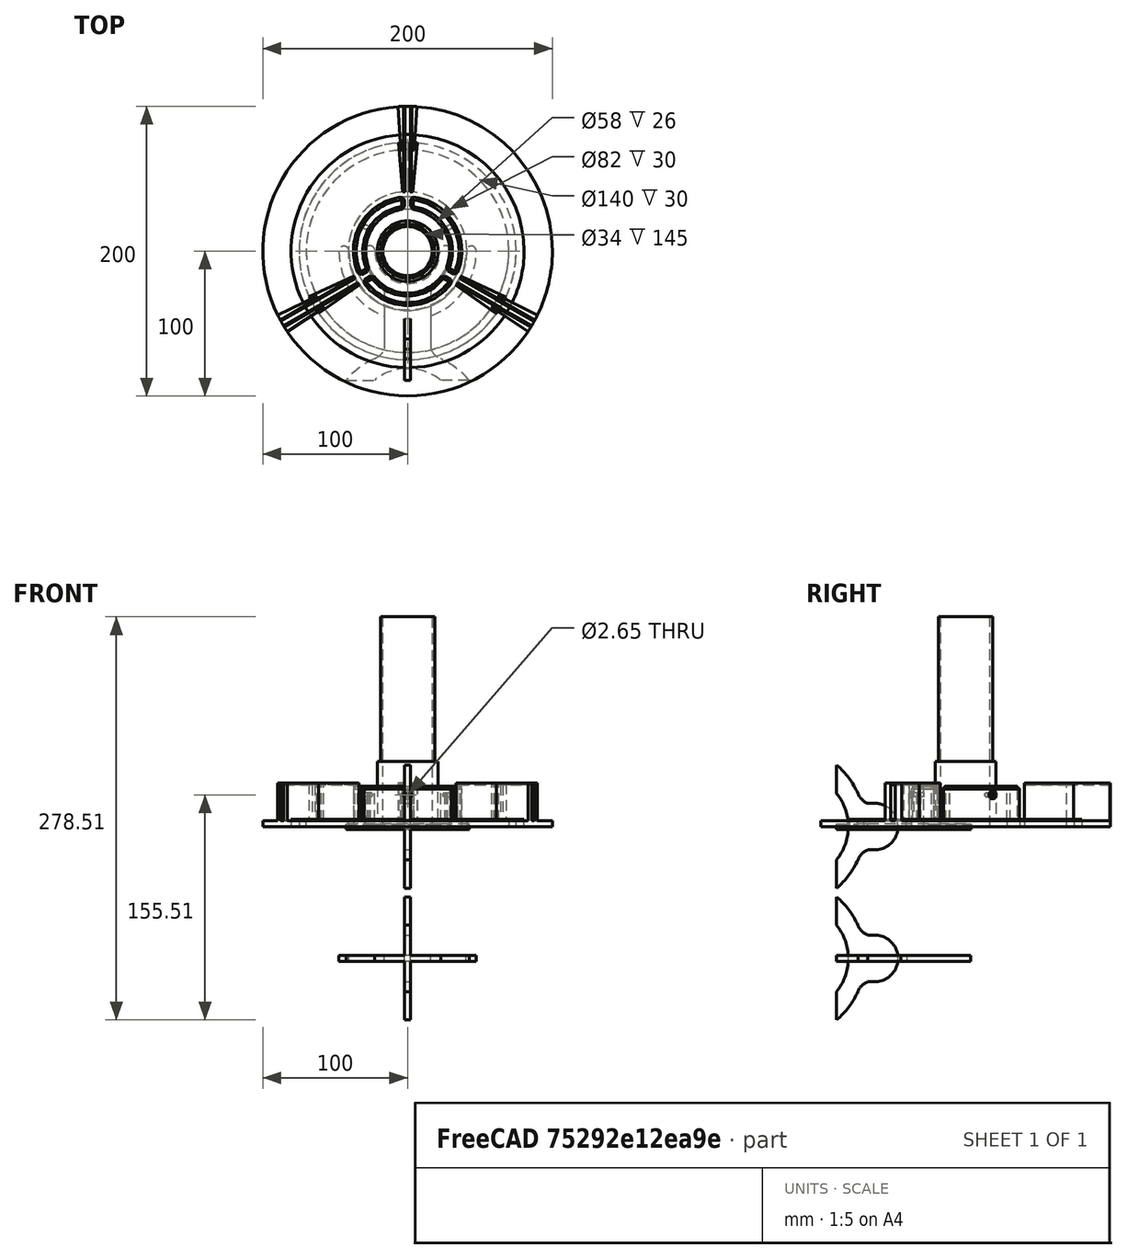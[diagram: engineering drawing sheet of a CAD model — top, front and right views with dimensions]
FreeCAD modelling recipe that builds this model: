
FCSTD DOCUMENT  (FreeCAD 1.0R39109 (Git))
Label: Madcow 3in Fiberglass Scooter Utility Set
License: All rights reserved
LicenseURL: http://en.wikipedia.org/wiki/All_rights_reserved
objects: Sketcher::SketchObject×23, PartDesign::Pocket×12, PartDesign::Pad×11, PartDesign::Body×9, App::Part×7, PartDesign::PolarPattern×6, PartDesign::Chamfer×6, PartDesign::Plane×2, Mesh::Feature×1
note: 156 computed .brp shape members not serialized (recipe doc carries the construction recipe); baked Part::Feature solids carry a one-line shape summary decoded from their .brp

FEATURE [Sketcher::SketchObject] Sketch
  ArcFitTolerance = 1e-06
  AttachmentSupport = -> [XY_Plane001]
  FullyConstrained = true
  MakeInternals = false
  MapMode = 5
  sketch-geometry (1):
    g0: Circle CenterX=0 CenterY=0 CenterZ=0 NormalX=0 NormalY=0 NormalZ=1 AngleXU=0 Radius=75
  constraints (2):
    c: Coincident(g0,g-1)
    c: Diameter(g0) = 150
FEATURE [PartDesign::Pad] Pad
  Direction = (0,0,1)
  Length = 30
  Length2 = 10
  Profile = -> Sketch
  ReferenceAxis = -> Sketch [N_Axis]
  Suppressed = false
  Type = 0
FEATURE [Sketcher::SketchObject] Sketch001
  ArcFitTolerance = 1e-06
  AttachmentSupport = -> [Pad]
  FullyConstrained = true
  MakeInternals = false
  MapMode = 5
  Placement = pos=(0,0,30) rot=(0,0,1;0rad)
  sketch-geometry (1):
    g0: Circle CenterX=0 CenterY=0 CenterZ=0 NormalX=0 NormalY=0 NormalZ=1 AngleXU=0 Radius=41
  constraints (2):
    c: Coincident(g0,g-1)
    c: Diameter(g0) = 82
FEATURE [PartDesign::Pocket] Pocket
  BaseFeature = -> Pad
  Direction = (0,0,-1)
  Length = 5
  Length2 = 5
  Profile = -> Sketch001
  ReferenceAxis = -> Sketch001 [N_Axis]
  Suppressed = false
  Type = 2
FEATURE [Sketcher::SketchObject] Sketch002
  ArcFitTolerance = 1e-06
  AttachmentSupport = -> [Pocket]
  FullyConstrained = false
  MakeInternals = false
  MapMode = 5
  Placement = pos=(0,0,30) rot=(0,0,1;0rad)
  sketch-geometry (4):
    g0: LineSegment StartX=-1.78365 StartY=75.7102 StartZ=0 EndX=-1.78365 EndY=37.8034 EndZ=0
    g1: LineSegment StartX=-1.78365 StartY=37.8034 StartZ=0 EndX=1.71635 EndY=37.8034 EndZ=0
    g2: LineSegment StartX=1.71635 StartY=37.8034 StartZ=0 EndX=1.71635 EndY=75.7102 EndZ=0
    g3: LineSegment StartX=1.71635 StartY=75.7102 StartZ=0 EndX=-1.78365 EndY=75.7102 EndZ=0
  constraints (9):
    c: Coincident(g0,g1)
    c: Coincident(g1,g2)
    c: Coincident(g2,g3)
    c: Coincident(g3,g0)
    c: Vertical(g0)
    c: Vertical(g2)
    c: Horizontal(g1)
    c: Horizontal(g3)
    c: DistanceX(g0,g2) = 3.5
FEATURE [PartDesign::Pocket] Pocket001
  BaseFeature = -> Pocket
  Direction = (0,0,-1)
  Length = 26
  Length2 = 5
  Profile = -> Sketch002
  ReferenceAxis = -> Sketch002 [N_Axis]
  Suppressed = false
  Type = 0
FEATURE [Sketcher::SketchObject] Sketch004
  ArcFitTolerance = 1e-06
  AttachmentSupport = -> [XY_Plane003]
  FullyConstrained = false
  MakeInternals = false
  MapMode = 5
  sketch-geometry (6):
    g0: Circle CenterX=0 CenterY=0 CenterZ=0 NormalX=0 NormalY=0 NormalZ=1 AngleXU=0 Radius=37.5
    g1: GeomPoint [constr] X=17.1424 Y=9.89717 Z=0
    g2: LineSegment [constr] StartX=0 StartY=0 StartZ=0 EndX=17.1424 EndY=9.89717 EndZ=0
    g3: LineSegment [constr] StartX=17.1424 StartY=9.89717 StartZ=0 EndX=32.476 EndY=18.75 EndZ=0
    g4: GeomPoint X=32.476 Y=18.75 Z=0
    g5: ArcOfCircle [constr] CenterX=0 CenterY=0 CenterZ=0 NormalX=0 NormalY=0 NormalZ=1 AngleXU=0 Radius=19.7943 StartAngle=0.523599 EndAngle=1.5708
  constraints (12):
    c: Coincident(g0,g-1)
    c: Diameter(g0) = 75
    c: Coincident(g2,g0)
    c: Coincident(g2,g1)
    c: Coincident(g3,g1)
    c: PointOnObject(g4,g0)
    c: Coincident(g3,g4)
    c: Coincident(g5,g0)
    c: Coincident(g5,g1)
    c: PointOnObject(g5,g-2)
    c: Perpendicular(g5,g3)
    c: Angle(g5) = 1.0472
FEATURE [PartDesign::Pad] Pad001
  Direction = (0,0,1)
  Length = 28
  Length2 = 10
  Profile = -> Sketch004
  ReferenceAxis = -> Sketch004 [N_Axis]
  Suppressed = false
  Type = 0
FEATURE [Sketcher::SketchObject] Sketch005
  ArcFitTolerance = 1e-06
  AttachmentSupport = -> [Pad001]
  FullyConstrained = true
  MakeInternals = false
  MapMode = 5
  Placement = pos=(0,0,28) rot=(0,0,1;0rad)
  sketch-geometry (1):
    g0: Circle CenterX=0 CenterY=0 CenterZ=0 NormalX=0 NormalY=0 NormalZ=1 AngleXU=0 Radius=29
  constraints (2):
    c: Coincident(g0,g-1)
    c: Diameter(g0) = 58
FEATURE [PartDesign::Pocket] Pocket003
  BaseFeature = -> Pad001
  Direction = (0,0,-1)
  Length = 5
  Length2 = 5
  Profile = -> Sketch005
  ReferenceAxis = -> Sketch005 [N_Axis]
  Suppressed = false
  Type = 2
FEATURE [Sketcher::SketchObject] Sketch006
  ArcFitTolerance = 1e-06
  AttachmentSupport = -> [Pocket003]
  FullyConstrained = false
  MakeInternals = false
  MapMode = 5
  Placement = pos=(0,0,28) rot=(0,0,1;0rad)
  sketch-geometry (4):
    g0: LineSegment StartX=-2.12501 StartY=38.7432 StartZ=0 EndX=-2.12501 EndY=23.0064 EndZ=0
    g1: LineSegment StartX=-2.12501 StartY=23.0064 StartZ=0 EndX=1.87499 EndY=23.0064 EndZ=0
    g2: LineSegment StartX=1.87499 StartY=23.0064 StartZ=0 EndX=1.87499 EndY=38.7432 EndZ=0
    g3: LineSegment StartX=1.87499 StartY=38.7432 StartZ=0 EndX=-2.12501 EndY=38.7432 EndZ=0
  constraints (9):
    c: Coincident(g0,g1)
    c: Coincident(g1,g2)
    c: Coincident(g2,g3)
    c: Coincident(g3,g0)
    c: Vertical(g0)
    c: Vertical(g2)
    c: Horizontal(g1)
    c: Horizontal(g3)
    c: DistanceX(g0,g2) = 4
FEATURE [PartDesign::Pocket] Pocket004
  BaseFeature = -> Pocket003
  Direction = (0,0,-1)
  Length = 24
  Length2 = 5
  Profile = -> Sketch006
  ReferenceAxis = -> Sketch006 [N_Axis]
  Suppressed = false
  Type = 0
FEATURE [PartDesign::PolarPattern] PolarPattern002
  Angle = 360
  Axis = -> Sketch006 [N_Axis]
  BaseFeature = -> Pocket004
  Mode = 0
  Occurrences = 3
  Offset = 120
  Originals = -> [Pocket004]
  Suppressed = false
  TransformMode = 0
FEATURE [PartDesign::Plane] DatumPlane
  AttachmentSupport = -> [Pocket003,Sketch004]
  Length = 117.19
  MapMode = 6
  Placement = pos=(32.476,18.75,0) rot=(0.377964,0.654654,0.654654;2.41886rad)
  ResizeMode = 0
  Width = 67.7376
FEATURE [Sketcher::SketchObject] Sketch007
  ArcFitTolerance = 1e-06
  AttachmentSupport = -> [DatumPlane]
  FullyConstrained = true
  MakeInternals = false
  MapMode = 5
  Placement = pos=(32.476,18.75,0) rot=(0.377964,0.654654,0.654654;2.41886rad)
  sketch-geometry (1):
    g0: Circle CenterX=0 CenterY=22 CenterZ=0 NormalX=0 NormalY=0 NormalZ=1 AngleXU=0 Radius=1.325
  constraints (3):
    c: PointOnObject(g0,g-2)
    c: Diameter(g0) = 2.65
    c: DistanceY(g-1,g0) = 22
FEATURE [PartDesign::Pocket] Pocket005
  BaseFeature = -> PolarPattern002
  Direction = (-0.866025,-0.5,1e-16)
  Length = 5
  Length2 = 5
  Profile = -> Sketch007
  ReferenceAxis = -> Sketch007 [N_Axis]
  Suppressed = false
  Type = 2
FEATURE [PartDesign::Chamfer] Chamfer
  Angle = 45
  Base = -> Pocket005 [Face7,Face3,Face11,Edge4,Edge6,Edge32,Edge37,Edge14,Edge12,Edge40,Edge44,Edge24,Edge29,Edge8,Edge10]
  BaseFeature = -> Pocket005
  ChamferType = 0
  FlipDirection = false
  Size = 2
  Size2 = 1
  SupportTransform = false
  Suppressed = false
  UseAllEdges = false
FEATURE [PartDesign::Chamfer] Chamfer001
  Angle = 45
  Base = -> Chamfer [Edge23]
  BaseFeature = -> Chamfer
  ChamferType = 0
  FlipDirection = false
  Size = 1.5
  Size2 = 1
  SupportTransform = false
  Suppressed = false
  UseAllEdges = false
FEATURE [PartDesign::PolarPattern] PolarPattern003
  Angle = 360
  Axis = -> Z_Axis003
  BaseFeature = -> Chamfer001
  Mode = 0
  Occurrences = 3
  Offset = 120
  Originals = -> [Pocket005,Chamfer001]
  Suppressed = false
  TransformMode = 0
FEATURE [PartDesign::Body] Body001
  AllowCompound = false
  Group = -> [Sketch004,Pad001,Sketch005,Pocket003,Sketch006,Pocket004,PolarPattern002,DatumPlane,Sketch007,Pocket005,Chamfer,Chamfer001,PolarPattern003]
  Origin = -> Origin003
  Tip = -> PolarPattern003
FEATURE [App::Part] Part001  label="Rear Rail Button Ring"
  Group = -> [Body001]
  Origin = -> Origin002
  Placement = pos=(0,0,17.3) rot=(0,0,1;0.532325rad)
FEATURE [Sketcher::SketchObject] Sketch008
  ArcFitTolerance = 1e-06
  AttachmentSupport = -> [XY_Plane005]
  FullyConstrained = false
  MakeInternals = false
  MapMode = 5
  sketch-geometry (2):
    g0: Circle CenterX=0 CenterY=0 CenterZ=0 NormalX=0 NormalY=0 NormalZ=1 AngleXU=0 Radius=38
    g1: GeomPoint X=32.9263 Y=-18.9699 Z=0
  constraints (3):
    c: Coincident(g0,g-1)
    c: Diameter(g0) = 76
    c: PointOnObject(g1,g0)
FEATURE [PartDesign::Pad] Pad002
  Direction = (0,0,1)
  Length = 20
  Length2 = 10
  Profile = -> Sketch008 [Edge1]
  ReferenceAxis = -> Sketch008 [N_Axis]
  Suppressed = false
  Type = 0
FEATURE [Sketcher::SketchObject] Sketch009
  ArcFitTolerance = 1e-06
  AttachmentSupport = -> [Pad002]
  FullyConstrained = true
  MakeInternals = false
  MapMode = 5
  Placement = pos=(0,0,20) rot=(0,0,1;0rad)
  sketch-geometry (1):
    g0: Circle CenterX=0 CenterY=0 CenterZ=0 NormalX=0 NormalY=0 NormalZ=1 AngleXU=0 Radius=29
  constraints (2):
    c: Coincident(g0,g-1)
    c: Diameter(g0) = 58
FEATURE [PartDesign::Pocket] Pocket006
  BaseFeature = -> Pad002
  Direction = (0,0,-1)
  Length = 5
  Length2 = 5
  Profile = -> Sketch009
  ReferenceAxis = -> Sketch009 [N_Axis]
  Suppressed = false
  Type = 2
FEATURE [PartDesign::Chamfer] Chamfer002
  Angle = 45
  Base = -> Pocket006 [Edge5,Edge4]
  BaseFeature = -> Pocket006
  ChamferType = 0
  FlipDirection = false
  Size = 4
  Size2 = 1
  SupportTransform = false
  Suppressed = false
  UseAllEdges = false
FEATURE [PartDesign::Plane] DatumPlane001
  AttachmentSupport = -> [Pad002,Sketch008]
  Length = 118.064
  MapMode = 6
  Placement = pos=(32.9263,-18.9699,0) rot=(0.774269,0.447497,0.447497;1.82389rad)
  ResizeMode = 0
  Width = 64.3989
FEATURE [Sketcher::SketchObject] Sketch010
  ArcFitTolerance = 1e-06
  AttachmentSupport = -> [DatumPlane001]
  FullyConstrained = false
  MakeInternals = false
  MapMode = 5
  Placement = pos=(32.9263,-18.9699,0) rot=(0.774269,0.447497,0.447497;1.82389rad)
  sketch-geometry (1):
    g0: Circle CenterX=0 CenterY=9.48073 CenterZ=0 NormalX=0 NormalY=0 NormalZ=1 AngleXU=0 Radius=1.325
  constraints (2):
    c: PointOnObject(g0,g-2)
    c: Diameter(g0) = 2.65
FEATURE [PartDesign::Pocket] Pocket007
  BaseFeature = -> Chamfer002
  Direction = (-0.866482,0.499208,1e-16)
  Length = 5
  Length2 = 5
  Profile = -> Sketch010
  ReferenceAxis = -> Sketch010 [N_Axis]
  Suppressed = false
  Type = 1
FEATURE [PartDesign::Chamfer] Chamfer003
  Angle = 45
  Base = -> Pocket007 [Edge8,Edge7]
  BaseFeature = -> Pocket007
  ChamferType = 0
  FlipDirection = false
  Size = 1.5
  Size2 = 1
  SupportTransform = false
  Suppressed = false
  UseAllEdges = false
FEATURE [PartDesign::Body] Body002
  AllowCompound = false
  Group = -> [Sketch008,Pad002,Sketch009,Pocket006,Chamfer002,DatumPlane001,Sketch010,Pocket007,Chamfer003]
  Origin = -> Origin005
  Tip = -> Chamfer003
FEATURE [App::Part] Part002  label="Front Rail Button Ring"
  Group = -> [Body002]
  Origin = -> Origin004
  Placement = pos=(0,0,468) rot=(0,0,1;1.55334rad)
FEATURE [Sketcher::SketchObject] Sketch011
  ArcFitTolerance = 1e-06
  AttachmentSupport = -> [XY_Plane007]
  FullyConstrained = false
  MakeInternals = false
  MapMode = 5
  sketch-geometry (21):
    g0: ArcOfCircle CenterX=0 CenterY=0 CenterZ=0 NormalX=0 NormalY=0 NormalZ=1 AngleXU=0 Radius=22.5 StartAngle=3.14159 EndAngle=6.28319
    g1: ArcOfCircle CenterX=0 CenterY=0 CenterZ=0 NormalX=0 NormalY=0 NormalZ=1 AngleXU=0 Radius=30 StartAngle=3.14159 EndAngle=4.14985
    g2: Circle [constr] CenterX=0 CenterY=0 CenterZ=0 NormalX=0 NormalY=0 NormalZ=1 AngleXU=0 Radius=39
    g3: ArcOfCircle CenterX=-26.25 CenterY=0 CenterZ=0 NormalX=0 NormalY=0 NormalZ=1 AngleXU=0 Radius=3.75 StartAngle=0 EndAngle=3.14159
    g4: LineSegment StartX=-16 StartY=-25.3772 StartZ=0 EndX=-16 EndY=-67.5009 EndZ=0
    g5: LineSegment [constr] StartX=-16 StartY=-51.3414 StartZ=0 EndX=-16 EndY=-74.3515 EndZ=0
    g6: LineSegment [constr] StartX=-16 StartY=-74.3515 StartZ=0 EndX=-39.0101 EndY=-74.3515 EndZ=0
    g7: LineSegment [constr] StartX=-16 StartY=-51.3414 StartZ=0 EndX=-39.0101 EndY=-74.3515 EndZ=0
    g8: GeomPoint [constr] X=-27.505 Y=-62.8465 Z=0
    g9: ArcOfCircle CenterX=-27.505 CenterY=-62.8465 CenterZ=0 NormalX=0 NormalY=0 NormalZ=1 AngleXU=0 Radius=12.4109 StartAngle=5.09682 EndAngle=5.89876
    g10: Circle [constr] CenterX=0 CenterY=0 CenterZ=0 NormalX=0 NormalY=0 NormalZ=1 AngleXU=0 Radius=92
    g11: ArcOfCircle CenterX=0 CenterY=-125.279 CenterZ=0 NormalX=0 NormalY=0 NormalZ=1 AngleXU=0 Radius=55.8188 StartAngle=1.99256 EndAngle=2.4365
    g12: LineSegment StartX=-42.5088 StartY=-89.1024 StartZ=0 EndX=-22.9079 EndY=-89.1024 EndZ=0
    g13: ArcOfCircle CenterX=0 CenterY=-117.403 CenterZ=0 NormalX=0 NormalY=0 NormalZ=1 AngleXU=0 Radius=36.4103 StartAngle=1.5708 EndAngle=2.25127
    g14: ArcOfCircle CenterX=0 CenterY=0 CenterZ=0 NormalX=0 NormalY=0 NormalZ=1 AngleXU=0 Radius=30 StartAngle=5.27493 EndAngle=6.28319
    g15: ArcOfCircle CenterX=26.25 CenterY=0 CenterZ=0 NormalX=0 NormalY=0 NormalZ=1 AngleXU=0 Radius=3.75 StartAngle=-2.22e-13 EndAngle=3.14159
    g16: LineSegment StartX=16 StartY=-25.3772 StartZ=0 EndX=16 EndY=-67.5009 EndZ=0
    g17: ArcOfCircle CenterX=27.505 CenterY=-62.8465 CenterZ=0 NormalX=0 NormalY=0 NormalZ=1 AngleXU=0 Radius=12.4109 StartAngle=3.52602 EndAngle=4.32796
    g18: ArcOfCircle CenterX=0 CenterY=-125.279 CenterZ=0 NormalX=0 NormalY=0 NormalZ=1 AngleXU=0 Radius=55.8188 StartAngle=0.705093 EndAngle=1.14903
    g19: LineSegment StartX=42.5088 StartY=-89.1024 StartZ=0 EndX=22.9079 EndY=-89.1024 EndZ=0
    g20: ArcOfCircle CenterX=0 CenterY=-117.403 CenterZ=0 NormalX=0 NormalY=0 NormalZ=1 AngleXU=0 Radius=36.4103 StartAngle=0.890327 EndAngle=1.5708
  constraints (58):
    c: Coincident(g0,g-1)
    c: PointOnObject(g0,g-1)
    c: PointOnObject(g0,g-1)
    c: Diameter(g0) = 45
    c: Coincident(g1,g0)
    c: PointOnObject(g1,g-1)
    c: Diameter(g1) = 60
    c: Coincident(g2,g0)
    c: Diameter(g2) = 78
    c: PointOnObject(g3,g-1)
    c: Coincident(g3,g1)
    c: Coincident(g3,g0)
    c: Coincident(g4,g1)
    c: Vertical(g4)
    c: Vertical(g5)
    c: Coincident(g6,g5)
    c: Horizontal(g6)
    c: Equal(g5,g6)
    c: Coincident(g7,g6)
    c: Symmetric(g7,g7,g8)
    c: Vertical(g5,g4)
    c: Coincident(g9,g8)
    c: Coincident(g9,g4)
    c: PointOnObject(g9,g6)
    c: Coincident(g7,g5)
    c: Coincident(g10,g0)
    c: Diameter(g10) = 184
    c: PointOnObject(g11,g-2)
    c: Coincident(g11,g9)
    c: Coincident(g12,g11)
    c: PointOnObject(g12,g10)
    c: Horizontal(g12)
    c: PointOnObject(g13,g-2)
    c: Coincident(g13,g12)
    c: PointOnObject(g13,g-2)
    c: Coincident(g14,g0)
    c: PointOnObject(g14,g-1)
    c: PointOnObject(g15,g-1)
    c: Coincident(g15,g0)
    c: Coincident(g15,g14)
    c: Symmetric(g15,g3,g-2)
    c: Symmetric(g1,g14,g-2)
    c: Symmetric(g1,g14,g-2)
    c: Coincident(g16,g14)
    c: Vertical(g16)
    c: Symmetric(g4,g16,g-2)
    c: Coincident(g17,g16)
    c: Symmetric(g17,g8,g-2)
    c: Symmetric(g9,g17,g-2)
    c: Coincident(g18,g11)
    c: Coincident(g18,g17)
    c: Symmetric(g11,g18,g-2)
    c: Coincident(g19,g18)
    c: Horizontal(g19)
    c: Coincident(g20,g13)
    c: Coincident(g20,g13)
    c: Coincident(g20,g19)
    c: DistanceX(g1,g14) = 32
FEATURE [PartDesign::Pad] Pad003
  Direction = (0,0,1)
  Length = 4
  Length2 = 10
  Midplane = true
  Profile = -> Sketch011
  ReferenceAxis = -> Sketch011 [N_Axis]
  Suppressed = false
  Type = 0
FEATURE [PartDesign::Body] Body003
  AllowCompound = false
  Group = -> [Sketch011,Pad003]
  Origin = -> Origin007
  Tip = -> Pad003
FEATURE [Sketcher::SketchObject] Sketch012
  ArcFitTolerance = 1e-06
  AttachmentSupport = -> [XY_Plane008]
  FullyConstrained = false
  MakeInternals = false
  MapMode = 5
  sketch-geometry (17):
    g0: Circle [constr] CenterX=0 CenterY=0 CenterZ=0 NormalX=0 NormalY=0 NormalZ=1 AngleXU=0 Radius=39
    g1: LineSegment StartX=-16 StartY=-60.6919 StartZ=0 EndX=-16 EndY=-67.5009 EndZ=0
    g2: LineSegment [constr] StartX=-16 StartY=-51.3415 StartZ=0 EndX=-16 EndY=-74.3516 EndZ=0
    g3: LineSegment [constr] StartX=-16 StartY=-74.3516 StartZ=0 EndX=-39.0101 EndY=-74.3516 EndZ=0
    g4: LineSegment [constr] StartX=-16 StartY=-51.3415 StartZ=0 EndX=-39.0101 EndY=-74.3516 EndZ=0
    g5: GeomPoint [constr] X=-27.505 Y=-62.8465 Z=0
    g6: ArcOfCircle CenterX=-27.505 CenterY=-62.8465 CenterZ=0 NormalX=0 NormalY=0 NormalZ=1 AngleXU=0 Radius=12.4109 StartAngle=5.09681 EndAngle=5.89876
    g7: Circle [constr] CenterX=2.1e-15 CenterY=1.67e-14 CenterZ=0 NormalX=0 NormalY=0 NormalZ=1 AngleXU=0 Radius=92
    g8: ArcOfCircle CenterX=0 CenterY=-125.279 CenterZ=0 NormalX=0 NormalY=0 NormalZ=1 AngleXU=0 Radius=55.8187 StartAngle=1.99256 EndAngle=2.4365
    g9: LineSegment StartX=-42.5088 StartY=-89.1024 StartZ=0 EndX=-22.9079 EndY=-89.1024 EndZ=0
    g10: ArcOfCircle CenterX=0 CenterY=-117.403 CenterZ=0 NormalX=0 NormalY=0 NormalZ=1 AngleXU=0 Radius=36.4103 StartAngle=1.5708 EndAngle=2.25127
    g11: LineSegment StartX=16 StartY=-60.6919 StartZ=0 EndX=16 EndY=-67.5009 EndZ=0
    g12: ArcOfCircle CenterX=27.505 CenterY=-62.8465 CenterZ=0 NormalX=0 NormalY=0 NormalZ=1 AngleXU=0 Radius=12.4109 StartAngle=3.52602 EndAngle=4.32797
    g13: ArcOfCircle CenterX=0 CenterY=-125.279 CenterZ=0 NormalX=0 NormalY=0 NormalZ=1 AngleXU=0 Radius=55.8187 StartAngle=0.705093 EndAngle=1.14903
    g14: LineSegment StartX=42.5088 StartY=-89.1024 StartZ=0 EndX=22.9079 EndY=-89.1024 EndZ=0
    g15: ArcOfCircle CenterX=0 CenterY=-117.403 CenterZ=0 NormalX=0 NormalY=0 NormalZ=1 AngleXU=0 Radius=36.4103 StartAngle=0.890327 EndAngle=1.5708
    g16: ArcOfCircle CenterX=1.1e-15 CenterY=-62.8718 CenterZ=0 NormalX=0 NormalY=0 NormalZ=1 AngleXU=0 Radius=16.1478 StartAngle=0.135404 EndAngle=3.00619
  constraints (41):
    c: Diameter(g0) = 78
    c: Vertical(g1)
    c: Vertical(g2)
    c: Coincident(g3,g2)
    c: Horizontal(g3)
    c: Equal(g2,g3)
    c: Coincident(g4,g3)
    c: Symmetric(g4,g4,g5)
    c: Vertical(g2,g1)
    c: Coincident(g6,g5)
    c: Coincident(g6,g1)
    c: PointOnObject(g6,g3)
    c: Coincident(g4,g2)
    c: Diameter(g7) = 184
    c: PointOnObject(g8,g-2)
    c: Coincident(g8,g6)
    c: Coincident(g9,g8)
    c: PointOnObject(g9,g7)
    c: Horizontal(g9)
    c: PointOnObject(g10,g-2)
    c: Coincident(g10,g9)
    c: PointOnObject(g10,g-2)
    c: Symmetric(g1,g11,g-2)
    c: Vertical(g11)
    c: Symmetric(g1,g11,g-2)
    c: Coincident(g12,g11)
    c: Symmetric(g12,g5,g-2)
    c: Symmetric(g6,g12,g-2)
    c: Coincident(g13,g8)
    c: Coincident(g13,g12)
    c: Symmetric(g8,g13,g-2)
    c: Coincident(g14,g13)
    c: Horizontal(g14)
    c: Coincident(g15,g10)
    c: Coincident(g15,g10)
    c: Coincident(g15,g14)
    c: DistanceX(g1,g11) = 32
    c: Horizontal(g1,g11)
    c: PointOnObject(g16,g-2)
    c: Coincident(g16,g1)
    c: Coincident(g16,g11)
FEATURE [PartDesign::Pad] Pad004
  Direction = (0,0,1)
  Length = 4
  Length2 = 10
  Midplane = true
  Profile = -> Sketch012
  ReferenceAxis = -> Sketch012 [N_Axis]
  Suppressed = false
  Type = 0
FEATURE [PartDesign::Body] Body004
  AllowCompound = false
  Group = -> [Sketch012,Pad004]
  Origin = -> Origin008
  Placement = pos=(0,0,0) rot=(0,1,0;1.5708rad)
  Tip = -> Pad004
FEATURE [App::Part] Part003  label="Rear Stand"
  Group = -> [Body003,Body004]
  Origin = -> Origin006
  Placement = pos=(0,0,-122.7) rot=(0,0,1;0rad)
FEATURE [Sketcher::SketchObject] Sketch013
  ArcFitTolerance = 1e-06
  AttachmentSupport = -> [XY_Plane010]
  FullyConstrained = false
  MakeInternals = false
  MapMode = 5
  sketch-geometry (21):
    g0: ArcOfCircle CenterX=0 CenterY=0 CenterZ=0 NormalX=0 NormalY=0 NormalZ=1 AngleXU=0 Radius=40.5 StartAngle=3.14159 EndAngle=6.28319
    g1: ArcOfCircle CenterX=0 CenterY=0 CenterZ=0 NormalX=0 NormalY=0 NormalZ=1 AngleXU=0 Radius=47.5 StartAngle=3.14159 EndAngle=4.36883
    g2: Circle [constr] CenterX=0 CenterY=0 CenterZ=0 NormalX=0 NormalY=0 NormalZ=1 AngleXU=0 Radius=39
    g3: ArcOfCircle CenterX=-44 CenterY=0 CenterZ=0 NormalX=0 NormalY=0 NormalZ=1 AngleXU=0 Radius=3.5 StartAngle=0 EndAngle=3.14159
    g4: LineSegment StartX=-16 StartY=-44.7242 StartZ=0 EndX=-16 EndY=-67.5009 EndZ=0
    g5: LineSegment [constr] StartX=-16 StartY=-51.3414 StartZ=0 EndX=-16 EndY=-74.3512 EndZ=0
    g6: LineSegment [constr] StartX=-16 StartY=-74.3512 StartZ=0 EndX=-39.0098 EndY=-74.3512 EndZ=0
    g7: LineSegment [constr] StartX=-16 StartY=-51.3414 StartZ=0 EndX=-39.0098 EndY=-74.3512 EndZ=0
    g8: GeomPoint [constr] X=-27.5049 Y=-62.8463 Z=0
    g9: ArcOfCircle CenterX=-27.5049 CenterY=-62.8463 CenterZ=0 NormalX=0 NormalY=0 NormalZ=1 AngleXU=0 Radius=12.4108 StartAngle=5.09684 EndAngle=5.89874
    g10: Circle [constr] CenterX=0 CenterY=0 CenterZ=0 NormalX=0 NormalY=0 NormalZ=1 AngleXU=0 Radius=92
    g11: ArcOfCircle CenterX=0 CenterY=-125.279 CenterZ=0 NormalX=0 NormalY=0 NormalZ=1 AngleXU=0 Radius=55.8189 StartAngle=1.99255 EndAngle=2.4365
    g12: LineSegment StartX=-42.5091 StartY=-89.1024 StartZ=0 EndX=-22.9079 EndY=-89.1024 EndZ=0
    g13: ArcOfCircle CenterX=0 CenterY=-117.403 CenterZ=0 NormalX=0 NormalY=0 NormalZ=1 AngleXU=0 Radius=36.4103 StartAngle=1.5708 EndAngle=2.25127
    g14: ArcOfCircle CenterX=0 CenterY=0 CenterZ=0 NormalX=0 NormalY=0 NormalZ=1 AngleXU=0 Radius=47.5 StartAngle=5.05595 EndAngle=6.28318
    g15: ArcOfCircle CenterX=44 CenterY=0 CenterZ=0 NormalX=0 NormalY=0 NormalZ=1 AngleXU=0 Radius=3.5 StartAngle=6.28316 EndAngle=9.42478
    g16: LineSegment StartX=16 StartY=-44.7242 StartZ=0 EndX=16 EndY=-67.5009 EndZ=0
    g17: ArcOfCircle CenterX=27.5049 CenterY=-62.8463 CenterZ=0 NormalX=0 NormalY=0 NormalZ=1 AngleXU=0 Radius=12.4108 StartAngle=3.52604 EndAngle=4.32794
    g18: ArcOfCircle CenterX=0 CenterY=-125.279 CenterZ=0 NormalX=0 NormalY=0 NormalZ=1 AngleXU=0 Radius=55.8189 StartAngle=0.705091 EndAngle=1.14904
    g19: LineSegment StartX=42.5091 StartY=-89.1024 StartZ=0 EndX=22.9079 EndY=-89.1024 EndZ=0
    g20: ArcOfCircle CenterX=0 CenterY=-117.403 CenterZ=0 NormalX=0 NormalY=0 NormalZ=1 AngleXU=0 Radius=36.4103 StartAngle=0.890327 EndAngle=1.5708
  constraints (58):
    c: Coincident(g0,g-1)
    c: PointOnObject(g0,g-1)
    c: PointOnObject(g0,g-1)
    c: Diameter(g0) = 81
    c: Coincident(g1,g0)
    c: PointOnObject(g1,g-1)
    c: Diameter(g1) = 95
    c: Coincident(g2,g0)
    c: Diameter(g2) = 78
    c: PointOnObject(g3,g-1)
    c: Coincident(g3,g1)
    c: Coincident(g3,g0)
    c: Coincident(g4,g1)
    c: Vertical(g4)
    c: Vertical(g5)
    c: Coincident(g6,g5)
    c: Horizontal(g6)
    c: Equal(g5,g6)
    c: Coincident(g7,g6)
    c: Symmetric(g7,g7,g8)
    c: Vertical(g5,g4)
    c: Coincident(g9,g8)
    c: Coincident(g9,g4)
    c: PointOnObject(g9,g6)
    c: Coincident(g7,g5)
    c: Coincident(g10,g0)
    c: Diameter(g10) = 184
    c: PointOnObject(g11,g-2)
    c: Coincident(g11,g9)
    c: Coincident(g12,g11)
    c: PointOnObject(g12,g10)
    c: Horizontal(g12)
    c: PointOnObject(g13,g-2)
    c: Coincident(g13,g12)
    c: PointOnObject(g13,g-2)
    c: Coincident(g14,g0)
    c: PointOnObject(g14,g-1)
    c: PointOnObject(g15,g-1)
    c: Coincident(g15,g0)
    c: Coincident(g15,g14)
    c: Symmetric(g15,g3,g-2)
    c: Symmetric(g1,g14,g-2)
    c: Symmetric(g1,g14,g-2)
    c: Coincident(g16,g14)
    c: Vertical(g16)
    c: Symmetric(g4,g16,g-2)
    c: Coincident(g17,g16)
    c: Symmetric(g17,g8,g-2)
    c: Symmetric(g9,g17,g-2)
    c: Coincident(g18,g11)
    c: Coincident(g18,g17)
    c: Symmetric(g11,g18,g-2)
    c: Coincident(g19,g18)
    c: Horizontal(g19)
    c: Coincident(g20,g13)
    c: Coincident(g20,g13)
    c: Coincident(g20,g19)
    c: DistanceX(g1,g14) = 32
FEATURE [PartDesign::Pad] Pad005
  Direction = (0,0,1)
  Length = 4
  Length2 = 10
  Midplane = true
  Profile = -> Sketch013
  ReferenceAxis = -> Sketch013 [N_Axis]
  Suppressed = false
  Type = 0
FEATURE [PartDesign::Body] Body005
  AllowCompound = false
  Group = -> [Sketch013,Pad005]
  Origin = -> Origin010
  Placement = pos=(0,0,-91) rot=(0,0,1;0rad)
  Tip = -> Pad005
FEATURE [Sketcher::SketchObject] Sketch014
  ArcFitTolerance = 1e-06
  AttachmentSupport = -> [XY_Plane011]
  FullyConstrained = false
  MakeInternals = false
  MapMode = 5
  sketch-geometry (17):
    g0: Circle [constr] CenterX=0 CenterY=0 CenterZ=0 NormalX=0 NormalY=0 NormalZ=1 AngleXU=0 Radius=39
    g1: LineSegment StartX=-16 StartY=-60.6919 StartZ=0 EndX=-16 EndY=-67.5009 EndZ=0
    g2: LineSegment [constr] StartX=-16 StartY=-51.3415 StartZ=0 EndX=-16 EndY=-74.3516 EndZ=0
    g3: LineSegment [constr] StartX=-16 StartY=-74.3516 StartZ=0 EndX=-39.0101 EndY=-74.3516 EndZ=0
    g4: LineSegment [constr] StartX=-16 StartY=-51.3415 StartZ=0 EndX=-39.0101 EndY=-74.3516 EndZ=0
    g5: GeomPoint [constr] X=-27.505 Y=-62.8465 Z=0
    g6: ArcOfCircle CenterX=-27.505 CenterY=-62.8465 CenterZ=0 NormalX=0 NormalY=0 NormalZ=1 AngleXU=0 Radius=12.4109 StartAngle=5.09681 EndAngle=5.89876
    g7: Circle [constr] CenterX=2.1e-15 CenterY=1.67e-14 CenterZ=0 NormalX=0 NormalY=0 NormalZ=1 AngleXU=0 Radius=92
    g8: ArcOfCircle CenterX=0 CenterY=-125.279 CenterZ=0 NormalX=0 NormalY=0 NormalZ=1 AngleXU=0 Radius=55.8187 StartAngle=1.99256 EndAngle=2.4365
    g9: LineSegment StartX=-42.5088 StartY=-89.1024 StartZ=0 EndX=-22.9079 EndY=-89.1024 EndZ=0
    g10: ArcOfCircle CenterX=0 CenterY=-117.403 CenterZ=0 NormalX=0 NormalY=0 NormalZ=1 AngleXU=0 Radius=36.4103 StartAngle=1.5708 EndAngle=2.25127
    g11: LineSegment StartX=16 StartY=-60.6919 StartZ=0 EndX=16 EndY=-67.5009 EndZ=0
    g12: ArcOfCircle CenterX=27.505 CenterY=-62.8465 CenterZ=0 NormalX=0 NormalY=0 NormalZ=1 AngleXU=0 Radius=12.4109 StartAngle=3.52602 EndAngle=4.32797
    g13: ArcOfCircle CenterX=0 CenterY=-125.279 CenterZ=0 NormalX=0 NormalY=0 NormalZ=1 AngleXU=0 Radius=55.8187 StartAngle=0.705093 EndAngle=1.14903
    g14: LineSegment StartX=42.5088 StartY=-89.1024 StartZ=0 EndX=22.9079 EndY=-89.1024 EndZ=0
    g15: ArcOfCircle CenterX=0 CenterY=-117.403 CenterZ=0 NormalX=0 NormalY=0 NormalZ=1 AngleXU=0 Radius=36.4103 StartAngle=0.890327 EndAngle=1.5708
    g16: ArcOfCircle CenterX=1.1e-15 CenterY=-62.8718 CenterZ=0 NormalX=0 NormalY=0 NormalZ=1 AngleXU=0 Radius=16.1478 StartAngle=0.135404 EndAngle=3.00619
  constraints (41):
    c: Diameter(g0) = 78
    c: Vertical(g1)
    c: Vertical(g2)
    c: Coincident(g3,g2)
    c: Horizontal(g3)
    c: Equal(g2,g3)
    c: Coincident(g4,g3)
    c: Symmetric(g4,g4,g5)
    c: Vertical(g2,g1)
    c: Coincident(g6,g5)
    c: Coincident(g6,g1)
    c: PointOnObject(g6,g3)
    c: Coincident(g4,g2)
    c: Diameter(g7) = 184
    c: PointOnObject(g8,g-2)
    c: Coincident(g8,g6)
    c: Coincident(g9,g8)
    c: PointOnObject(g9,g7)
    c: Horizontal(g9)
    c: PointOnObject(g10,g-2)
    c: Coincident(g10,g9)
    c: PointOnObject(g10,g-2)
    c: Symmetric(g1,g11,g-2)
    c: Vertical(g11)
    c: Symmetric(g1,g11,g-2)
    c: Coincident(g12,g11)
    c: Symmetric(g12,g5,g-2)
    c: Symmetric(g6,g12,g-2)
    c: Coincident(g13,g8)
    c: Coincident(g13,g12)
    c: Symmetric(g8,g13,g-2)
    c: Coincident(g14,g13)
    c: Horizontal(g14)
    c: Coincident(g15,g10)
    c: Coincident(g15,g10)
    c: Coincident(g15,g14)
    c: DistanceX(g1,g11) = 32
    c: Horizontal(g1,g11)
    c: PointOnObject(g16,g-2)
    c: Coincident(g16,g1)
    c: Coincident(g16,g11)
FEATURE [PartDesign::Pad] Pad006
  Direction = (0,0,1)
  Length = 4
  Length2 = 10
  Midplane = true
  Profile = -> Sketch014
  ReferenceAxis = -> Sketch014 [N_Axis]
  Suppressed = false
  Type = 0
FEATURE [PartDesign::Body] Body006
  AllowCompound = false
  Group = -> [Sketch014,Pad006]
  Origin = -> Origin011
  Placement = pos=(2.02e-14,0,-91) rot=(0,1,0;1.5708rad)
  Tip = -> Pad006
FEATURE [Mesh::Feature] fg_scooter30
  Placement = pos=(37,0,0) rot=(0,0,1;0rad)
FEATURE [App::Part] Part004  label="Front Stand"
  Group = -> [Body006,Body005]
  Origin = -> Origin012
  Placement = pos=(0,0,447.5) rot=(0,0,1;0rad)
FEATURE [PartDesign::Chamfer] Chamfer004
  Angle = 45
  Base = -> Pocket001 [Edge12,Edge9]
  BaseFeature = -> Pocket001
  ChamferType = 0
  FlipDirection = false
  Size = 1
  Size2 = 1
  SupportTransform = false
  Suppressed = false
  UseAllEdges = false
FEATURE [PartDesign::PolarPattern] PolarPattern
  Angle = 360
  Axis = -> Sketch002 [N_Axis]
  BaseFeature = -> Chamfer004
  Mode = 0
  Occurrences = 3
  Offset = 120
  Originals = -> [Pocket001,Chamfer004]
  Suppressed = false
  TransformMode = 0
FEATURE [Sketcher::SketchObject] Sketch003
  ArcFitTolerance = 1e-06
  AttachmentSupport = -> [PolarPattern]
  FullyConstrained = false
  MakeInternals = false
  MapMode = 5
  Placement = pos=(0,0,30) rot=(0,0,1;0rad)
  sketch-geometry (4):
    g0: ArcOfCircle CenterX=0 CenterY=0 CenterZ=0 NormalX=0 NormalY=0 NormalZ=1 AngleXU=0 Radius=78.29 StartAngle=5.84346 EndAngle=7.76332
    g1: ArcOfCircle CenterX=0 CenterY=0 CenterZ=0 NormalX=0 NormalY=0 NormalZ=1 AngleXU=0 Radius=40 StartAngle=5.84346 EndAngle=7.76332
    g2: LineSegment StartX=7.08794 StartY=77.9685 StartZ=0 EndX=3.62138 EndY=39.8357 EndZ=0
    g3: LineSegment StartX=70.8422 StartY=-33.3273 StartZ=0 EndX=36.1948 EndY=-17.0276 EndZ=0
  constraints (11):
    c: Coincident(g0,g-1)
    c: Coincident(g1,g0)
    c: Radius(g0) = 78.29
    c: Radius(g1) = 40
    c: Angle(g0) = 1.91986
    c: Coincident(g2,g0)
    c: Coincident(g2,g1)
    c: Perpendicular(g0,g2)
    c: Coincident(g3,g0)
    c: Coincident(g3,g1)
    c: Perpendicular(g0,g3)
FEATURE [PartDesign::Pocket] Pocket002
  BaseFeature = -> PolarPattern
  Direction = (0,0,-1)
  Length = 26
  Length2 = 5
  Profile = -> Sketch003
  ReferenceAxis = -> Sketch003 [N_Axis]
  Suppressed = false
  Type = 0
FEATURE [PartDesign::PolarPattern] PolarPattern001
  Angle = 360
  Axis = -> Sketch003 [N_Axis]
  BaseFeature = -> Pocket002
  Mode = 0
  Occurrences = 3
  Offset = 120
  Originals = -> [Pocket002]
  Suppressed = false
  TransformMode = 0
FEATURE [PartDesign::Body] Body
  AllowCompound = false
  Group = -> [Sketch,Pad,Sketch001,Pocket,Sketch002,Pocket001,Chamfer004,PolarPattern,Sketch003,Pocket002,PolarPattern001]
  Origin = -> Origin001
  Tip = -> PolarPattern001
FEATURE [App::Part] Part  label="Fin Hoder Rear"
  Group = -> [Body]
  Origin = -> Origin
  Placement = pos=(0,0,-9.2) rot=(0,0,1;0.514872rad)
FEATURE [Sketcher::SketchObject] Sketch015
  ArcFitTolerance = 1e-06
  AttachmentSupport = -> [XY_Plane014]
  FullyConstrained = true
  MakeInternals = false
  MapMode = 5
  sketch-geometry (1):
    g0: Circle CenterX=0 CenterY=0 CenterZ=0 NormalX=0 NormalY=0 NormalZ=1 AngleXU=0 Radius=100
  constraints (2):
    c: Coincident(g0,g-1)
    c: Diameter(g0) = 200
FEATURE [PartDesign::Pad] Pad007
  Direction = (0,0,1)
  Length = 30
  Length2 = 10
  Profile = -> Sketch015
  ReferenceAxis = -> Sketch015 [N_Axis]
  Suppressed = false
  Type = 0
FEATURE [Sketcher::SketchObject] Sketch016
  ArcFitTolerance = 1e-06
  AttachmentSupport = -> [Pad007]
  FullyConstrained = true
  MakeInternals = false
  MapMode = 5
  Placement = pos=(0,0,30) rot=(0,0,1;0rad)
  sketch-geometry (1):
    g0: Circle CenterX=0 CenterY=0 CenterZ=0 NormalX=0 NormalY=0 NormalZ=1 AngleXU=0 Radius=70
  constraints (2):
    c: Coincident(g0,g-1)
    c: Diameter(g0) = 140
FEATURE [PartDesign::Pocket] Pocket008
  BaseFeature = -> Pad007
  Direction = (0,0,-1)
  Length = 5
  Length2 = 5
  Profile = -> Sketch016
  ReferenceAxis = -> Sketch016 [N_Axis]
  Suppressed = false
  Type = 2
FEATURE [Sketcher::SketchObject] Sketch017
  ArcFitTolerance = 1e-06
  AttachmentSupport = -> [Pocket008]
  FullyConstrained = false
  MakeInternals = false
  MapMode = 5
  Placement = pos=(0,0,30) rot=(0,0,1;0rad)
  sketch-geometry (4):
    g0: LineSegment StartX=-1.66772 StartY=100.019 StartZ=0 EndX=-1.66772 EndY=37.8034 EndZ=0
    g1: LineSegment StartX=-1.66772 StartY=37.8034 StartZ=0 EndX=1.83228 EndY=37.8034 EndZ=0
    g2: LineSegment StartX=1.83228 StartY=37.8034 StartZ=0 EndX=1.83228 EndY=100.019 EndZ=0
    g3: LineSegment StartX=1.83228 StartY=100.019 StartZ=0 EndX=-1.66772 EndY=100.019 EndZ=0
  constraints (9):
    c: Coincident(g0,g1)
    c: Coincident(g1,g2)
    c: Coincident(g2,g3)
    c: Coincident(g3,g0)
    c: Vertical(g0)
    c: Vertical(g2)
    c: Horizontal(g1)
    c: Horizontal(g3)
    c: DistanceX(g0,g2) = 3.5
FEATURE [PartDesign::Pocket] Pocket009
  BaseFeature = -> Pocket008
  Direction = (0,0,-1)
  Length = 26
  Length2 = 5
  Profile = -> Sketch017
  ReferenceAxis = -> Sketch017 [N_Axis]
  Suppressed = false
  Type = 0
FEATURE [PartDesign::Chamfer] Chamfer005
  Angle = 45
  Base = -> Pocket009 [Edge12,Edge9]
  BaseFeature = -> Pocket009
  ChamferType = 0
  FlipDirection = false
  Size = 1
  Size2 = 1
  SupportTransform = false
  Suppressed = false
  UseAllEdges = false
FEATURE [PartDesign::PolarPattern] PolarPattern004
  Angle = 360
  Axis = -> Sketch017 [N_Axis]
  BaseFeature = -> Chamfer005
  Mode = 0
  Occurrences = 3
  Offset = 120
  Originals = -> [Pocket009,Chamfer005]
  Suppressed = false
  TransformMode = 0
FEATURE [Sketcher::SketchObject] Sketch018
  ArcFitTolerance = 1e-06
  AttachmentSupport = -> [PolarPattern004]
  FullyConstrained = false
  MakeInternals = false
  MapMode = 5
  Placement = pos=(0,0,30) rot=(0,0,1;0rad)
  sketch-geometry (4):
    g0: ArcOfCircle CenterX=0 CenterY=0 CenterZ=0 NormalX=0 NormalY=0 NormalZ=1 AngleXU=0 Radius=110 StartAngle=5.82594 EndAngle=7.78943
    g1: ArcOfCircle CenterX=0 CenterY=0 CenterZ=0 NormalX=0 NormalY=0 NormalZ=1 AngleXU=0 Radius=40 StartAngle=5.82594 EndAngle=7.78943
    g2: LineSegment StartX=7.0952 StartY=109.771 StartZ=0 EndX=2.58007 EndY=39.9167 EndZ=0
    g3: LineSegment StartX=98.6999 StartY=-48.5626 StartZ=0 EndX=35.8909 EndY=-17.6591 EndZ=0
  constraints (11):
    c: Coincident(g0,g-1)
    c: Coincident(g1,g0)
    c: Radius(g0) = 110
    c: Radius(g1) = 40
    c: Angle(g0) = 1.9635
    c: Coincident(g2,g0)
    c: Coincident(g2,g1)
    c: Perpendicular(g0,g2)
    c: Coincident(g3,g0)
    c: Coincident(g3,g1)
    c: Perpendicular(g0,g3)
FEATURE [PartDesign::Pocket] Pocket010
  BaseFeature = -> PolarPattern004
  Direction = (0,0,-1)
  Length = 26
  Length2 = 5
  Profile = -> Sketch018
  ReferenceAxis = -> Sketch018 [N_Axis]
  Suppressed = false
  Type = 0
FEATURE [PartDesign::PolarPattern] PolarPattern005
  Angle = 360
  Axis = -> Sketch018 [N_Axis]
  BaseFeature = -> Pocket010
  Mode = 0
  Occurrences = 3
  Offset = 120
  Originals = -> [Pocket010]
  Suppressed = false
  TransformMode = 0
FEATURE [PartDesign::Body] Body007
  AllowCompound = false
  Group = -> [Sketch015,Pad007,Sketch016,Pocket008,Sketch017,Pocket009,Chamfer005,PolarPattern004,Sketch018,Pocket010,PolarPattern005]
  Origin = -> Origin014
  Tip = -> PolarPattern005
FEATURE [App::Part] Part005  label="Fin Hoder Front"
  Group = -> [Body007]
  Origin = -> Origin013
  Placement = pos=(0.524682,-0.927373,112.895) rot=(0.965921,-0.258818,-0.003058;3.14782rad)
FEATURE [Sketcher::SketchObject] Sketch019
  ArcFitTolerance = 1e-06
  AttachmentSupport = -> [XY_Plane016]
  FullyConstrained = false
  MakeInternals = false
  MapMode = 5
  sketch-geometry (1):
    g0: Circle CenterX=0 CenterY=0 CenterZ=0 NormalX=0 NormalY=0 NormalZ=1 AngleXU=0 Radius=80.4566
  constraints (1):
    c: Coincident(g0,g-1)
FEATURE [PartDesign::Pad] Pad008
  Direction = (0,0,1)
  Length = 5
  Length2 = 10
  Profile = -> Sketch019
  ReferenceAxis = -> Sketch019 [N_Axis]
  Suppressed = false
  Type = 0
FEATURE [Sketcher::SketchObject] Sketch020
  ArcFitTolerance = 1e-06
  AttachmentSupport = -> [Pad008]
  FullyConstrained = true
  MakeInternals = false
  MapMode = 5
  Placement = pos=(0,0,5) rot=(0,0,1;0rad)
  sketch-geometry (1):
    g0: Circle CenterX=0 CenterY=0 CenterZ=0 NormalX=0 NormalY=0 NormalZ=1 AngleXU=0 Radius=21
  constraints (2):
    c: Coincident(g0,g-1)
    c: Diameter(g0) = 42
FEATURE [PartDesign::Pad] Pad009
  BaseFeature = -> Pad008
  Direction = (0,0,1)
  Length = 40
  Length2 = 10
  Profile = -> Sketch020
  ReferenceAxis = -> Sketch020 [N_Axis]
  Suppressed = false
  Type = 0
FEATURE [Sketcher::SketchObject] Sketch021
  ArcFitTolerance = 1e-06
  AttachmentSupport = -> [Pad009]
  FullyConstrained = true
  MakeInternals = false
  MapMode = 5
  Placement = pos=(0,0,45) rot=(0,0,1;0rad)
  sketch-geometry (1):
    g0: Circle CenterX=0 CenterY=0 CenterZ=0 NormalX=0 NormalY=0 NormalZ=1 AngleXU=0 Radius=18.75
  constraints (2):
    c: Coincident(g0,g-1)
    c: Diameter(g0) = 37.5
FEATURE [PartDesign::Pad] Pad010
  BaseFeature = -> Pad009
  Direction = (0,0,1)
  Length = 100
  Length2 = 10
  Profile = -> Sketch021
  ReferenceAxis = -> Sketch021 [N_Axis]
  Suppressed = false
  Type = 0
FEATURE [Sketcher::SketchObject] Sketch022
  ArcFitTolerance = 1e-06
  AttachmentSupport = -> [Pad010]
  FullyConstrained = true
  MakeInternals = false
  MapMode = 5
  Placement = pos=(0,0,145) rot=(0,0,1;0rad)
  sketch-geometry (1):
    g0: Circle CenterX=0 CenterY=0 CenterZ=0 NormalX=0 NormalY=0 NormalZ=1 AngleXU=0 Radius=17
  constraints (2):
    c: Coincident(g0,g-1)
    c: Diameter(g0) = 34
FEATURE [PartDesign::Pocket] Pocket011
  BaseFeature = -> Pad010
  Direction = (0,0,-1)
  Length = 5
  Length2 = 5
  Profile = -> Sketch022
  ReferenceAxis = -> Sketch022 [N_Axis]
  Suppressed = false
  Type = 1
FEATURE [PartDesign::Body] Body008
  AllowCompound = false
  Group = -> [Sketch019,Pad008,Sketch020,Pad009,Sketch021,Pad010,Sketch022,Pocket011]
  Origin = -> Origin016
  Tip = -> Pocket011
FEATURE [App::Part] Part006  label="Painting Stand"
  Group = -> [Body008]
  Origin = -> Origin015
  Placement = pos=(0,0,-291.2) rot=(0,0,1;0rad)
